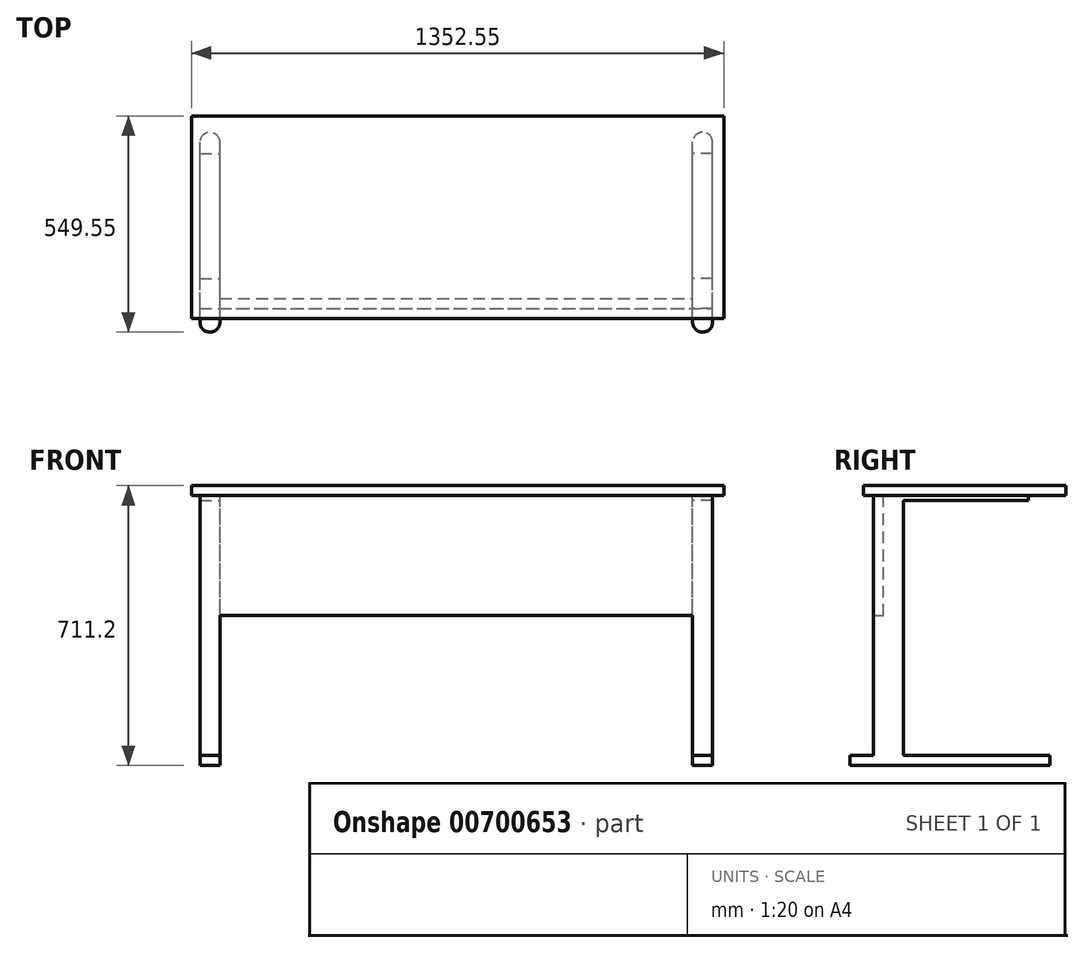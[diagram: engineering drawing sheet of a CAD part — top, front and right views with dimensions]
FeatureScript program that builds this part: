
annotation { "Feature Type Name" : "Feature", "Feature Type Description" : "" }
export const myFeature = defineFeature(function(context is Context, id is Id, definition is map)
    precondition{}
    {
        {
            var Q0;
            Q0=qCreatedBy(makeId("Top.planeOp"),FACE);
            var sketch = newSketch(context, id + "F0", { "sketchPlane" : qUnion([Q0])});
            skLineSegment(sketch, "E0.bottom", {"start": v(-672.97, 172.9) * mm, "end": v(679.58, 172.9) * mm});
            skLineSegment(sketch, "E0.top", {"start": v(-672.97, -341.44) * mm, "end": v(679.58, -341.44) * mm});
            skLineSegment(sketch, "E0.left", {"start": v(-672.97, 172.9) * mm, "end": v(-672.97, -341.44) * mm});
            skLineSegment(sketch, "E0.right", {"start": v(679.58, 172.9) * mm, "end": v(679.58, -341.44) * mm});
            skSolve(sketch);
        }
        {
            var Q0;
            Q0 = qSketchRegion(id + "F0", true);
            extrude(context, id + "F1", {"entities" : qUnion([Q0]), "depth" : 25.4 * mm, "offsetDistance" : 25.4 * mm});
        }
        {
            var Q0;
            Q0=makeQuery(id+"F1.opExtrude","CAP_FACE",FACE,{"disambiguationData":[OSD([sQuery(id+"F0.wireOp",EDGE,"E0.bottom"),sQuery(id+"F0.wireOp",EDGE,"E0.top"),sQuery(id+"F0.wireOp",EDGE,"E0.left"),sQuery(id+"F0.wireOp",EDGE,"E0.right")])],"isStart":false});
            var sketch = newSketch(context, id + "F2", { "sketchPlane" : qUnion([Q0])});
            skLineSegment(sketch, "E1.bottom", {"start": v(-651.36, -239.84) * mm, "end": v(-600.56, -239.84) * mm});
            skLineSegment(sketch, "E1.top", {"start": v(-651.36, 77.66) * mm, "end": v(-600.56, 77.66) * mm});
            skLineSegment(sketch, "E1.left", {"start": v(-651.36, -239.84) * mm, "end": v(-651.36, 77.66) * mm});
            skLineSegment(sketch, "E1.right", {"start": v(-600.56, -239.84) * mm, "end": v(-600.56, 77.66) * mm});
            skLineSegment(sketch, "E2.MirrorCS", {"start": v(600.56, -239.84) * mm, "end": v(600.56, 77.66) * mm});
            skLineSegment(sketch, "E3.MirrorCS", {"start": v(651.36, 77.66) * mm, "end": v(600.56, 77.66) * mm});
            skLineSegment(sketch, "E4.MirrorCS", {"start": v(651.36, -239.84) * mm, "end": v(651.36, 77.66) * mm});
            skLineSegment(sketch, "E5.MirrorCS", {"start": v(651.36, -239.84) * mm, "end": v(600.56, -239.84) * mm});
            skSolve(sketch);
        }
        {
            var Q0;
            Q0 = qSketchRegion(id + "F2", true);
            extrude(context, id + "F3", {"entities" : qUnion([Q0]), "operationType" : NewBodyOperationType.ADD, "oppositeDirection" : true, "depth" : 38.1 * mm, "offsetDistance" : 25.4 * mm});
        }
        {
            var Q0;
            Q0=makeQuery(id+"F1.opExtrude","CAP_FACE",FACE,{"disambiguationData":[OSD([sQuery(id+"F0.wireOp",EDGE,"E0.bottom"),sQuery(id+"F0.wireOp",EDGE,"E0.top"),sQuery(id+"F0.wireOp",EDGE,"E0.left"),sQuery(id+"F0.wireOp",EDGE,"E0.right")])],"isStart":true});
            var sketch = newSketch(context, id + "F4", { "sketchPlane" : qUnion([Q0])});
            skLineSegment(sketch, "E6.bottom", {"start": v(-651.36, 239.84) * mm, "end": v(-600.56, 239.84) * mm});
            skLineSegment(sketch, "E6.top", {"start": v(-651.36, 316.04) * mm, "end": v(-600.56, 316.04) * mm});
            skLineSegment(sketch, "E6.left", {"start": v(-651.36, 239.84) * mm, "end": v(-651.36, 316.04) * mm});
            skLineSegment(sketch, "E6.right", {"start": v(-600.56, 239.84) * mm, "end": v(-600.56, 316.04) * mm});
            skLineSegment(sketch, "E7.MirrorCS", {"start": v(600.56, 239.84) * mm, "end": v(600.56, 316.04) * mm});
            skLineSegment(sketch, "E8.MirrorCS", {"start": v(651.36, 239.84) * mm, "end": v(600.56, 239.84) * mm});
            skLineSegment(sketch, "E9.MirrorCS", {"start": v(651.36, 239.84) * mm, "end": v(651.36, 316.04) * mm});
            skLineSegment(sketch, "E10.MirrorCS", {"start": v(651.36, 316.04) * mm, "end": v(600.56, 316.04) * mm});
            skSolve(sketch);
        }
        {
            var Q0;
            Q0 = qSketchRegion(id + "F4", true);
            extrude(context, id + "F5", {"entities" : qUnion([Q0]), "operationType" : NewBodyOperationType.ADD, "depth" : 660.4 * mm, "offsetDistance" : 25.4 * mm});
        }
        {
            var Q0;
            Q0=makeQuery(id+"F5.opExtrude","CAP_FACE",FACE,{"disambiguationData":[OSD([sQuery(id+"F4.wireOp",EDGE,"E7.MirrorCS"),sQuery(id+"F4.wireOp",EDGE,"E8.MirrorCS"),sQuery(id+"F4.wireOp",EDGE,"E9.MirrorCS"),sQuery(id+"F4.wireOp",EDGE,"E10.MirrorCS")])],"isStart":false});
            var sketch = newSketch(context, id + "F6", { "sketchPlane" : qUnion([Q0])});
            skLineSegment(sketch, "E11.bottom", {"start": v(651.36, 376.64) * mm, "end": v(600.56, 376.64) * mm});
            skLineSegment(sketch, "E11.top", {"start": v(651.36, -131.36) * mm, "end": v(600.56, -131.36) * mm});
            skLineSegment(sketch, "E11.left", {"start": v(651.36, 376.64) * mm, "end": v(651.36, -131.36) * mm});
            skLineSegment(sketch, "E11.right", {"start": v(600.56, 376.64) * mm, "end": v(600.56, -131.36) * mm});
            skLineSegment(sketch, "E12.MirrorCS", {"start": v(-600.56, 376.64) * mm, "end": v(-600.56, -131.36) * mm});
            skLineSegment(sketch, "E13.MirrorCS", {"start": v(-651.36, 376.64) * mm, "end": v(-651.36, -131.36) * mm});
            skLineSegment(sketch, "E14.MirrorCS", {"start": v(-651.36, -131.36) * mm, "end": v(-600.56, -131.36) * mm});
            skLineSegment(sketch, "E15.MirrorCS", {"start": v(-651.36, 376.64) * mm, "end": v(-600.56, 376.64) * mm});
            skSolve(sketch);
        }
        {
            var Q0;
            Q0 = qSketchRegion(id + "F6", true);
            extrude(context, id + "F7", {"entities" : qUnion([Q0]), "operationType" : NewBodyOperationType.ADD, "depth" : 25.4 * mm, "offsetDistance" : 25.4 * mm});
        }
        {
            var Q0;
            Q0=makeQuery(id+"F7.opExtrude","SWEPT_EDGE",EDGE,{"disambiguationData":[OSD([sQuery(id+"F6.wireOp",EDGE,"E11.top"),sQuery(id+"F6.wireOp",EDGE,"E11.left")])]});
            fillet(context, id + "F8", {"entities" : qUnion([Q0]), "radius" : 25.4 * mm, "tangentPropagation" : true, "allowEdgeOverflow" : false});
        }
        {
            var Q0;
            Q0=makeQuery(id+"F7.opExtrude","SWEPT_EDGE",EDGE,{"disambiguationData":[OSD([sQuery(id+"F6.wireOp",EDGE,"E11.top"),sQuery(id+"F6.wireOp",EDGE,"E11.right")])]});
            fillet(context, id + "F9", {"entities" : qUnion([Q0]), "radius" : 25.4 * mm, "tangentPropagation" : true, "allowEdgeOverflow" : false});
        }
        {
            var Q0;
            Q0=makeQuery(id+"F7.opExtrude","SWEPT_EDGE",EDGE,{"disambiguationData":[OSD([sQuery(id+"F6.wireOp",EDGE,"E11.bottom"),sQuery(id+"F6.wireOp",EDGE,"E11.left")])]});
            fillet(context, id + "F10", {"entities" : qUnion([Q0]), "radius" : 25.4 * mm, "tangentPropagation" : true, "allowEdgeOverflow" : false});
        }
        {
            var Q0;
            Q0=makeQuery(id+"F7.opExtrude","SWEPT_EDGE",EDGE,{"disambiguationData":[OSD([sQuery(id+"F6.wireOp",EDGE,"E11.bottom"),sQuery(id+"F6.wireOp",EDGE,"E11.right")])]});
            fillet(context, id + "F11", {"entities" : qUnion([Q0]), "radius" : 25.4 * mm, "tangentPropagation" : true, "allowEdgeOverflow" : false});
        }
        {
            var Q0;
            Q0=makeQuery(id+"F7.opExtrude","SWEPT_EDGE",EDGE,{"disambiguationData":[OSD([sQuery(id+"F6.wireOp",EDGE,"E12.MirrorCS"),sQuery(id+"F6.wireOp",EDGE,"E15.MirrorCS")])]});
            var Q1;
            Q1=makeQuery(id+"F7.opExtrude","SWEPT_EDGE",EDGE,{"disambiguationData":[OSD([sQuery(id+"F6.wireOp",EDGE,"E13.MirrorCS"),sQuery(id+"F6.wireOp",EDGE,"E15.MirrorCS")])]});
            fillet(context, id + "F12", {"entities" : qUnion([Q0, Q1]), "radius" : 25.4 * mm, "tangentPropagation" : true, "allowEdgeOverflow" : false});
        }
        {
            var Q0;
            Q0=makeQuery(id+"F7.opExtrude","SWEPT_EDGE",EDGE,{"disambiguationData":[OSD([sQuery(id+"F6.wireOp",EDGE,"E13.MirrorCS"),sQuery(id+"F6.wireOp",EDGE,"E14.MirrorCS")])]});
            var Q1;
            Q1=makeQuery(id+"F7.opExtrude","SWEPT_EDGE",EDGE,{"disambiguationData":[OSD([sQuery(id+"F6.wireOp",EDGE,"E12.MirrorCS"),sQuery(id+"F6.wireOp",EDGE,"E14.MirrorCS")])]});
            fillet(context, id + "F13", {"entities" : qUnion([Q0, Q1]), "radius" : 25.4 * mm, "tangentPropagation" : true, "allowEdgeOverflow" : false});
        }
        {
            var Q0;
            Q0=makeQuery(id+"F1.opExtrude","CAP_FACE",FACE,{"disambiguationData":[OSD([sQuery(id+"F0.wireOp",EDGE,"E0.bottom"),sQuery(id+"F0.wireOp",EDGE,"E0.top"),sQuery(id+"F0.wireOp",EDGE,"E0.left"),sQuery(id+"F0.wireOp",EDGE,"E0.right")])],"isStart":true});
            var sketch = newSketch(context, id + "F14", { "sketchPlane" : qUnion([Q0])});
            skLineSegment(sketch, "E16.bottom", {"start": v(-600.56, 316.04) * mm, "end": v(600.56, 316.04) * mm});
            skLineSegment(sketch, "E16.top", {"start": v(-600.56, 290.64) * mm, "end": v(600.56, 290.64) * mm});
            skLineSegment(sketch, "E16.left", {"start": v(-600.56, 316.04) * mm, "end": v(-600.56, 290.64) * mm});
            skLineSegment(sketch, "E16.right", {"start": v(600.56, 316.04) * mm, "end": v(600.56, 290.64) * mm});
            skSolve(sketch);
        }
        {
            var Q0;
            Q0 = qSketchRegion(id + "F14", true);
            extrude(context, id + "F15", {"entities" : qUnion([Q0]), "operationType" : NewBodyOperationType.ADD, "depth" : 304.8 * mm, "offsetDistance" : 25.4 * mm});
        }
    });
